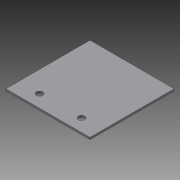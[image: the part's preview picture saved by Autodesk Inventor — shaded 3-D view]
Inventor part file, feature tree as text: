
AUTODESK INVENTOR PART (.ipt)
format: ipt  version: 2015 (Build 190159000, 159)  size: 83,968 bytes
history: native  units: mm
features: extrude x2, sketch x2, other x1
ambient origin geometry x8: Origin, YZ Plane, XZ Plane, XY Plane, X Axis, Y Axis, Z Axis, Center Point
bodies: Body1 (feature_tree)
feature tree (5):
  other  "ソリッド1"
  extrude  "押し出し1"  Depth=40.0mm
  extrude  "押し出し2"  Depth=40.0mm
  sketch  "スケッチ1"
  sketch  "スケッチ2"
